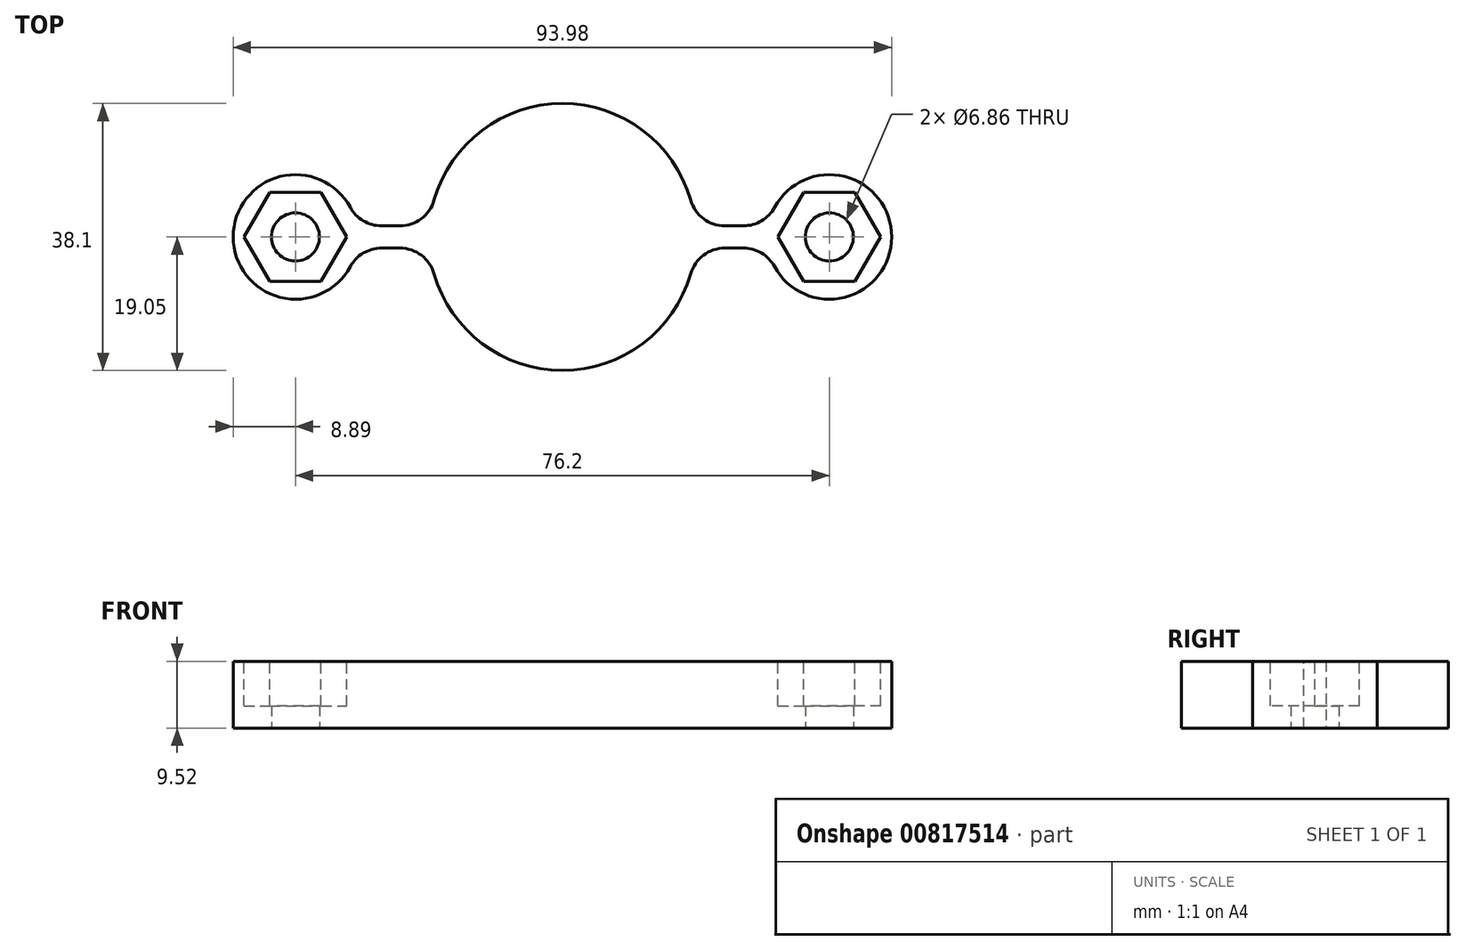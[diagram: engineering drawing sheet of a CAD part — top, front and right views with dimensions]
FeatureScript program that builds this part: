
annotation { "Feature Type Name" : "Feature", "Feature Type Description" : "" }
export const myFeature = defineFeature(function(context is Context, id is Id, definition is map)
    precondition{}
    {
        {
            var Q0;
            Q0=qCreatedBy(makeId("Top.planeOp"),FACE);
            var sketch = newSketch(context, id + "F0", { "sketchPlane" : qUnion([Q0])});
            skArc(sketch, "E0", {"start": v(-18.98, -1.59) * mm, "mid": v(0, -19.05) * mm, "end": v(18.98, -1.59) * mm});
            skArc(sketch, "E1", {"start": v(-29.35, 1.59) * mm, "mid": v(-47, 0) * mm, "end": v(-29.35, -1.59) * mm});
            skArc(sketch, "E2", {"start": v(29.35, -1.59) * mm, "mid": v(47, 0) * mm, "end": v(29.35, 1.59) * mm});
            skLineSegment(sketch, "E3.bottom", {"start": v(-29.35, 1.59) * mm, "end": v(-18.98, 1.59) * mm});
            skLineSegment(sketch, "E3.top", {"start": v(-29.35, -1.59) * mm, "end": v(-18.98, -1.59) * mm});
            skLineSegment(sketch, "E4.bottom", {"start": v(18.98, 1.59) * mm, "end": v(29.35, 1.59) * mm});
            skLineSegment(sketch, "E4.top", {"start": v(18.98, -1.59) * mm, "end": v(29.35, -1.59) * mm});
            skArc(sketch, "E5.trimOffspring", {"start": v(18.98, 1.59) * mm, "mid": v(0, 19.05) * mm, "end": v(-18.98, 1.59) * mm});
            skSolve(sketch);
        }
        {
            var Q0;
            Q0 = qSketchRegion(id + "F0", true);
            extrude(context, id + "F1", {"entities" : qUnion([Q0]), "endBound" : BoundingType.SYMMETRIC, "depth" : 9.52 * mm, "offsetDistance" : 25.4 * mm});
        }
        {
            var Q0;
            Q0=makeQuery(id+"F1.opExtrude","SWEPT_EDGE",EDGE,{"disambiguationData":[OSD([sQuery(id+"F0.wireOp",EDGE,"E1"),sQuery(id+"F0.wireOp",EDGE,"E3.bottom")])]});
            var Q1;
            Q1=makeQuery(id+"F1.opExtrude","SWEPT_EDGE",EDGE,{"disambiguationData":[OSD([sQuery(id+"F0.wireOp",EDGE,"E4.bottom"),sQuery(id+"F0.wireOp",EDGE,"E5.trimOffspring")])]});
            var Q2;
            Q2=makeQuery(id+"F1.opExtrude","SWEPT_EDGE",EDGE,{"disambiguationData":[OSD([sQuery(id+"F0.wireOp",EDGE,"E3.bottom"),sQuery(id+"F0.wireOp",EDGE,"E5.trimOffspring")])]});
            var Q3;
            Q3=makeQuery(id+"F1.opExtrude","SWEPT_EDGE",EDGE,{"disambiguationData":[OSD([sQuery(id+"F0.wireOp",EDGE,"E2"),sQuery(id+"F0.wireOp",EDGE,"E4.bottom")])]});
            var Q4;
            Q4=makeQuery(id+"F1.opExtrude","SWEPT_EDGE",EDGE,{"disambiguationData":[OSD([sQuery(id+"F0.wireOp",EDGE,"E2"),sQuery(id+"F0.wireOp",EDGE,"E4.top")])]});
            var Q5;
            Q5=makeQuery(id+"F1.opExtrude","SWEPT_EDGE",EDGE,{"disambiguationData":[OSD([sQuery(id+"F0.wireOp",EDGE,"E0"),sQuery(id+"F0.wireOp",EDGE,"E3.top")])]});
            var Q6;
            Q6=makeQuery(id+"F1.opExtrude","SWEPT_EDGE",EDGE,{"disambiguationData":[OSD([sQuery(id+"F0.wireOp",EDGE,"E1"),sQuery(id+"F0.wireOp",EDGE,"E3.top")])]});
            var Q7;
            Q7=makeQuery(id+"F1.opExtrude","SWEPT_EDGE",EDGE,{"disambiguationData":[OSD([sQuery(id+"F0.wireOp",EDGE,"E0"),sQuery(id+"F0.wireOp",EDGE,"E4.top")])]});
            fillet(context, id + "F2", {"entities" : qUnion([Q0, Q1, Q2, Q3, Q4, Q5, Q6, Q7]), "radius" : 5.08 * mm, "tangentPropagation" : true, "allowEdgeOverflow" : false});
        }
        {
            var Q0;
            Q0=makeQuery(id+"F1.opExtrude","CAP_FACE",FACE,{"disambiguationData":[OSD([sQuery(id+"F0.wireOp",EDGE,"E0"),sQuery(id+"F0.wireOp",EDGE,"E1"),sQuery(id+"F0.wireOp",EDGE,"E2"),sQuery(id+"F0.wireOp",EDGE,"E3.bottom"),sQuery(id+"F0.wireOp",EDGE,"E3.top"),sQuery(id+"F0.wireOp",EDGE,"E4.bottom"),sQuery(id+"F0.wireOp",EDGE,"E4.top"),sQuery(id+"F0.wireOp",EDGE,"E5.trimOffspring")])],"isStart":false});
            var sketch = newSketch(context, id + "F3", { "sketchPlane" : qUnion([Q0])});
            skCircle(sketch, "E6.cCircle", {"center": v(-38.1, 0) * mm, "radius": 6.35 * mm, "construction": true});
            skLineSegment(sketch, "E6.0", {"start": v(-34.43, 6.35) * mm, "end": v(-30.77, 0) * mm});
            skLineSegment(sketch, "E6.1", {"start": v(-30.77, 0) * mm, "end": v(-34.43, -6.35) * mm});
            skLineSegment(sketch, "E6.2", {"start": v(-34.43, -6.35) * mm, "end": v(-41.77, -6.35) * mm});
            skLineSegment(sketch, "E6.3", {"start": v(-41.77, -6.35) * mm, "end": v(-45.43, 0) * mm});
            skLineSegment(sketch, "E6.4", {"start": v(-45.43, 0) * mm, "end": v(-41.77, 6.35) * mm});
            skLineSegment(sketch, "E6.5", {"start": v(-41.77, 6.35) * mm, "end": v(-34.43, 6.35) * mm});
            skPoint(sketch, "E6.0.midPoint", {"position": v(-32.6, 3.18) * mm});
            skCircle(sketch, "E7.cCircle", {"center": v(38.1, 0) * mm, "radius": 6.35 * mm, "construction": true});
            skLineSegment(sketch, "E7.0", {"start": v(45.43, 0) * mm, "end": v(41.77, -6.35) * mm});
            skLineSegment(sketch, "E7.1", {"start": v(41.77, -6.35) * mm, "end": v(34.43, -6.35) * mm});
            skLineSegment(sketch, "E7.2", {"start": v(34.43, -6.35) * mm, "end": v(30.77, 0) * mm});
            skLineSegment(sketch, "E7.3", {"start": v(30.77, 0) * mm, "end": v(34.43, 6.35) * mm});
            skLineSegment(sketch, "E7.4", {"start": v(34.43, 6.35) * mm, "end": v(41.77, 6.35) * mm});
            skLineSegment(sketch, "E7.5", {"start": v(41.77, 6.35) * mm, "end": v(45.43, 0) * mm});
            skPoint(sketch, "E7.0.midPoint", {"position": v(43.6, -3.17) * mm});
            skSolve(sketch);
        }
        {
            var Q0;
            Q0 = qSketchRegion(id + "F3", true);
            extrude(context, id + "F4", {"entities" : qUnion([Q0]), "operationType" : NewBodyOperationType.REMOVE, "oppositeDirection" : true, "depth" : 6.35 * mm, "offsetDistance" : 25.4 * mm});
        }
        {
            var Q0;
            Q0=makeQuery(id+"F1.opExtrude","CAP_FACE",FACE,{"disambiguationData":[OSD([sQuery(id+"F0.wireOp",EDGE,"E0"),sQuery(id+"F0.wireOp",EDGE,"E1"),sQuery(id+"F0.wireOp",EDGE,"E2"),sQuery(id+"F0.wireOp",EDGE,"E3.bottom"),sQuery(id+"F0.wireOp",EDGE,"E3.top"),sQuery(id+"F0.wireOp",EDGE,"E4.bottom"),sQuery(id+"F0.wireOp",EDGE,"E4.top"),sQuery(id+"F0.wireOp",EDGE,"E5.trimOffspring")])],"isStart":true});
            var sketch = newSketch(context, id + "F5", { "sketchPlane" : qUnion([Q0])});
            skCircle(sketch, "E8", {"center": v(-38.1, 0) * mm, "radius": 3.43 * mm});
            skCircle(sketch, "E9", {"center": v(38.1, 0) * mm, "radius": 3.43 * mm});
            skSolve(sketch);
        }
        {
            var Q0;
            Q0 = qSketchRegion(id + "F5", true);
            extrude(context, id + "F6", {"entities" : qUnion([Q0]), "operationType" : NewBodyOperationType.REMOVE, "endBound" : BoundingType.THROUGH_ALL, "oppositeDirection" : true, "depth" : 25.4 * mm, "offsetDistance" : 25.4 * mm});
        }
    });
